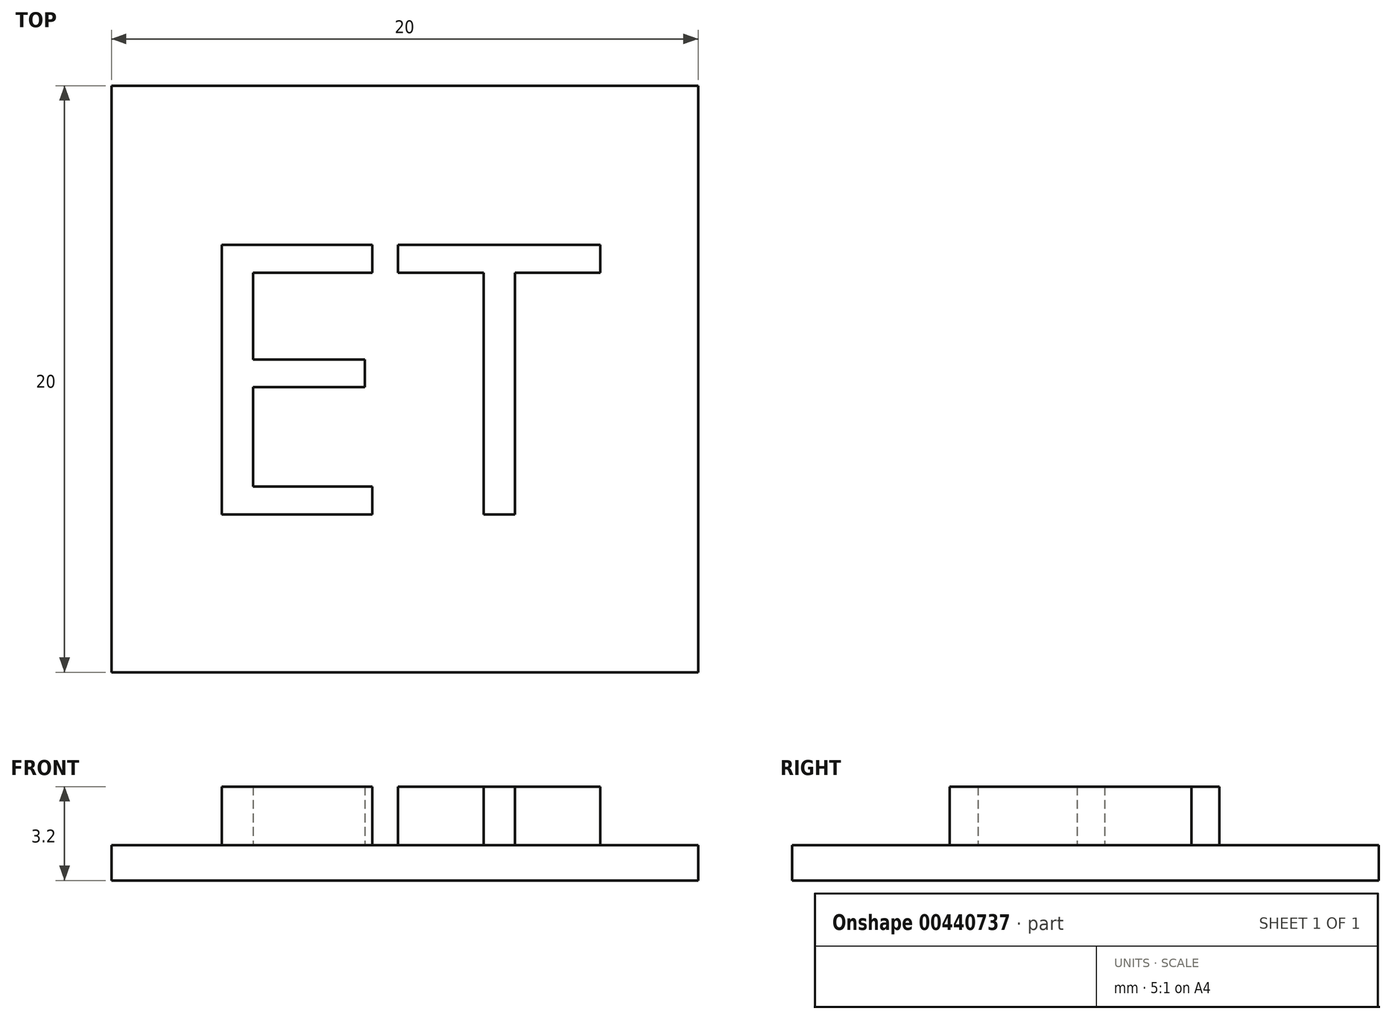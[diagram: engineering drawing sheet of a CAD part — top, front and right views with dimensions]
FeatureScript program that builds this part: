
annotation { "Feature Type Name" : "Feature", "Feature Type Description" : "" }
export const myFeature = defineFeature(function(context is Context, id is Id, definition is map)
    precondition{}
    {
        {
            var Q0;
            Q0=qCreatedBy(makeId("Top.planeOp"),FACE);
            var sketch = newSketch(context, id + "F0", { "sketchPlane" : qUnion([Q0])});
            skLineSegment(sketch, "E0.bottom", {"start": v(10, 10) * mm, "end": v(-10, 10) * mm});
            skLineSegment(sketch, "E0.top", {"start": v(10, -10) * mm, "end": v(-10, -10) * mm});
            skLineSegment(sketch, "E0.left", {"start": v(10, 10) * mm, "end": v(10, -10) * mm});
            skLineSegment(sketch, "E0.right", {"start": v(-10, 10) * mm, "end": v(-10, -10) * mm});
            skPoint(sketch, "E0.middle", {"position": v(0, 0) * mm});
            skSolve(sketch);
        }
        {
            var Q0;
            Q0 = qSketchRegion(id + "F0", true);
            extrude(context, id + "F1", {"entities" : qUnion([Q0]), "depth" : 1.2 * mm});
        }
        {
            var Q0;
            Q0=makeQuery(id+"F1.opExtrude","CAP_FACE",FACE,{"disambiguationData":[OSD([sQuery(id+"F0.wireOp",EDGE,"E0.bottom"),sQuery(id+"F0.wireOp",EDGE,"E0.top"),sQuery(id+"F0.wireOp",EDGE,"E0.left"),sQuery(id+"F0.wireOp",EDGE,"E0.right")])],"isStart":false});
            var sketch = newSketch(context, id + "F2", { "sketchPlane" : qUnion([Q0])});
            skText(sketch, "E1", { "text": "ET", "fontName": "OpenSans-Regular.ttf"});
            const initialGuessF2  = {"E1": [-0.0075, -0.00462, 1, 0, 0.00927]};
            skSetInitialGuess(sketch, initialGuessF2);
            skSolve(sketch);
        }
        {
            var Q0;
            Q0 = qSketchRegion(id + "F2", true);
            extrude(context, id + "F3", {"entities" : qUnion([Q0]), "operationType" : NewBodyOperationType.ADD, "depth" : 2 * mm});
        }
    });
